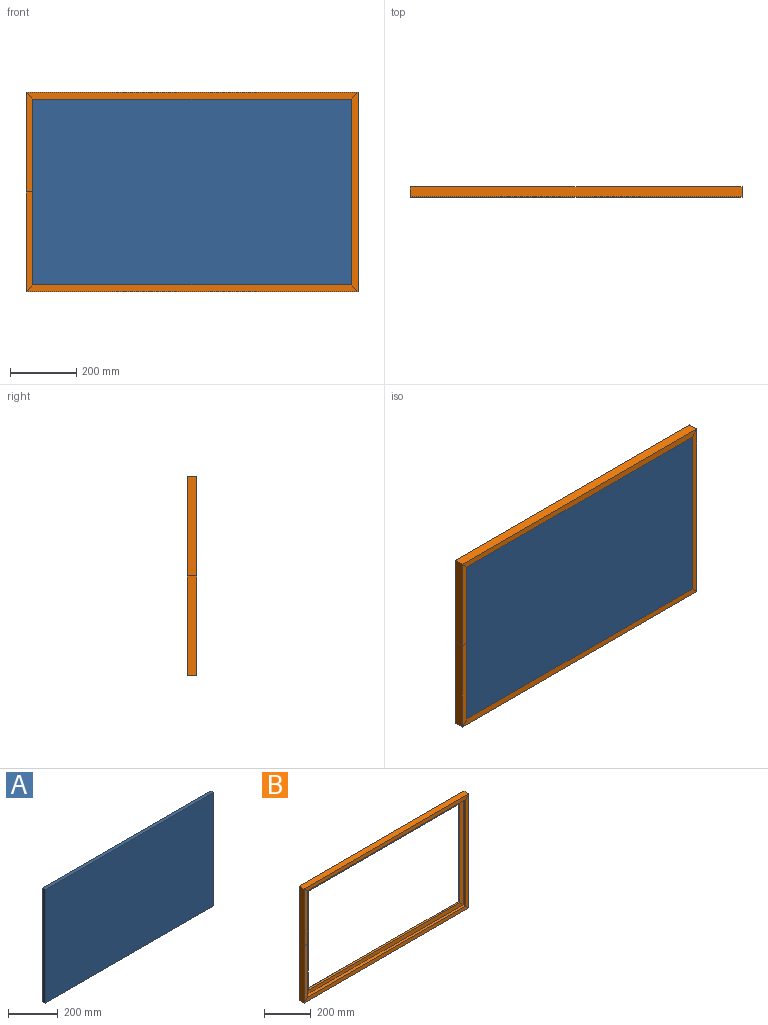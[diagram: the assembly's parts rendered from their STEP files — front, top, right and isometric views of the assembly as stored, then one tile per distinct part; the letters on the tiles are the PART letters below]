
ASSEMBLY  parts=2 mates=1
PART A: 6 faces, bbox 960x15x560 mm
  f0: plane 960x560mm, normal (0,-1,0), area 537600mm2, adj f1,f2,f3,f5
  f1: plane 960x15mm, normal (0,0,-1), area 14400mm2, adj f0,f2,f4,f5
  f2: plane 560x15mm, normal (-1,0,0), area 8400mm2, adj f0,f1,f3,f4
  f3: plane 960x15mm, normal (0,0,1), area 14400mm2, adj f0,f2,f4,f5
  f4: plane 960x560mm, normal (0,1,0), area 537600mm2, adj f1,f2,f3,f5
  f5: plane 560x15mm, normal (1,0,0), area 8400mm2, adj f0,f1,f3,f4
PART B: 35 faces, bbox 1000x30x600 mm
  f0: plane 1000x30mm, normal (0,0,-1), area 30000mm2, adj f2,f3,f9,f21
  f1: plane 960x15mm, normal (0,0,1), area 14400mm2, adj f2,f6,f7,f22
  f2: plane 1000x20mm, normal (0,-1,0), area 19600mm2, adj f0,f1,f8,f23
  f3: plane 1000x35mm, normal (0,1,0), area 33775mm2, adj f0,f4,f10,f24
  f4: plane 930x5mm, normal (0,0.71,0.71), area 6540.7mm2, adj f3,f5,f11,f25
  f5: plane 920x10mm, normal (0,0,1), area 9200mm2, adj f4,f6,f12,f26
  f6: plane 960x20mm, normal (0,-1,0), area 18800mm2, adj f1,f5,f13,f27
  f7: plane 280x15mm, normal (1,0,0), area 4200mm2, adj f1,f8,f13,f15
  f8: plane 300x20mm, normal (0,-1,0), area 5800mm2, adj f2,f7,f9,f16
  f9: plane 300x30mm, normal (-1,0,0), area 9000mm2, adj f0,f8,f10,f14
  f10: plane 300x35mm, normal (0,1,0), area 9887.5mm2, adj f3,f9,f11,f17
  f11: plane 265x5mm, normal (0.71,0.71,0), area 1856.2mm2, adj f4,f10,f12,f18
  f12: plane 260x10mm, normal (1,0,0), area 2600mm2, adj f5,f11,f13,f19
  f13: plane 280x20mm, normal (0,-1,0), area 5400mm2, adj f6,f7,f12,f20
  f14: plane 300x30mm, normal (-1,0,0), area 9000mm2, adj f9,f16,f17,f28
  f15: plane 280x15mm, normal (1,0,0), area 4200mm2, adj f7,f16,f20,f29
  f16: plane 300x20mm, normal (0,-1,0), area 5800mm2, adj f8,f14,f15,f30
  f17: plane 300x35mm, normal (0,1,0), area 9887.5mm2, adj f10,f14,f18,f31
  f18: plane 265x5mm, normal (0.71,0.71,0), area 1856.2mm2, adj f11,f17,f19,f32
  f19: plane 260x10mm, normal (1,0,0), area 2600mm2, adj f12,f18,f20,f33
  f20: plane 280x20mm, normal (0,-1,0), area 5400mm2, adj f13,f15,f19,f34
  f21: plane 600x30mm, normal (1,0,0), area 18000mm2, adj f0,f23,f24,f28
  f22: plane 560x15mm, normal (-1,0,0), area 8400mm2, adj f1,f23,f27,f29
  f23: plane 600x20mm, normal (0,-1,0), area 11600mm2, adj f2,f21,f22,f30
  f24: plane 600x35mm, normal (0,1,0), area 19775mm2, adj f3,f21,f25,f31
  f25: plane 530x5mm, normal (-0.71,0.71,0), area 3712.3mm2, adj f4,f24,f26,f32
  f26: plane 520x10mm, normal (-1,0,0), area 5200mm2, adj f5,f25,f27,f33
  f27: plane 560x20mm, normal (0,-1,0), area 10800mm2, adj f6,f22,f26,f34
  f28: plane 1000x30mm, normal (0,0,1), area 30000mm2, adj f14,f21,f30,f31
  f29: plane 960x15mm, normal (0,0,-1), area 14400mm2, adj f15,f22,f30,f34
  f30: plane 1000x20mm, normal (0,-1,0), area 19600mm2, adj f16,f23,f28,f29
  f31: plane 1000x35mm, normal (0,1,0), area 33775mm2, adj f17,f24,f28,f32
  f32: plane 930x5mm, normal (0,0.71,-0.71), area 6540.7mm2, adj f18,f25,f31,f33
  f33: plane 920x10mm, normal (0,0,-1), area 9200mm2, adj f19,f26,f32,f34
  f34: plane 960x20mm, normal (0,-1,0), area 18800mm2, adj f20,f27,f29,f33
PLACE A at identity
PLACE B at identity
MATE fastened A.f5 <-> B.f22  axis (-1,0,0) through (-7841.7,9201.11,2409.75)mm
